# Revit family: Sinks-Overmount-Clark Horizon 1.75 end bowl
name_source: partatom
category: Plumbing Fixtures
revit_build: Autodesk Revit 2015 (Build: 20140606_1530(x64)
units: mm (PartAtom-declared; Revit-internal decimal feet)

## types (1)
- Standard
    Assembly Code = D2010410
    CW Connection = No
    Cost = 0 $
    Default Elevation = 0 mm  [stored 0 ft]
    Depth = 183 mm
    Description = 1200mm (L) 500mm (W) 183mm (D)/Premium 304 Grade Stainless Steel/overmount
    HW Connection = No
    HoleAlignment = 482 mm  [stored 1.58136 ft]
    HoleDiameter = 35 mm  [stored 0.114829 ft]
    Length = 1200 mm  [stored 3.93701 ft]
    Manufacturer = GWA Bathrooms & Kitchens
    Material_ANZRS = Metal-Stainless-Caroma
    Model = HR3107
    ModifiedIssue_ANZRS = 20160630.54 $
    TapHoleSpacing = 26 mm
    TapPenetration = 150 mm
    Type Comments = Horizon 1.75 end bowl sink
    URL = http://specify.caroma.com.au
    Vent Connection = No
    WFU = 2
    Waste Connection = Yes
    Width = 500 mm  [stored 1.64042 ft]

note: [stored X ft] marks values corroborated as IEEE doubles in the binary element streams (Revit-internal decimal feet)

## geometry (parser evidence)
native form markers: Blend x12, Sweep x2
no freeform markers — native parametric forms only
